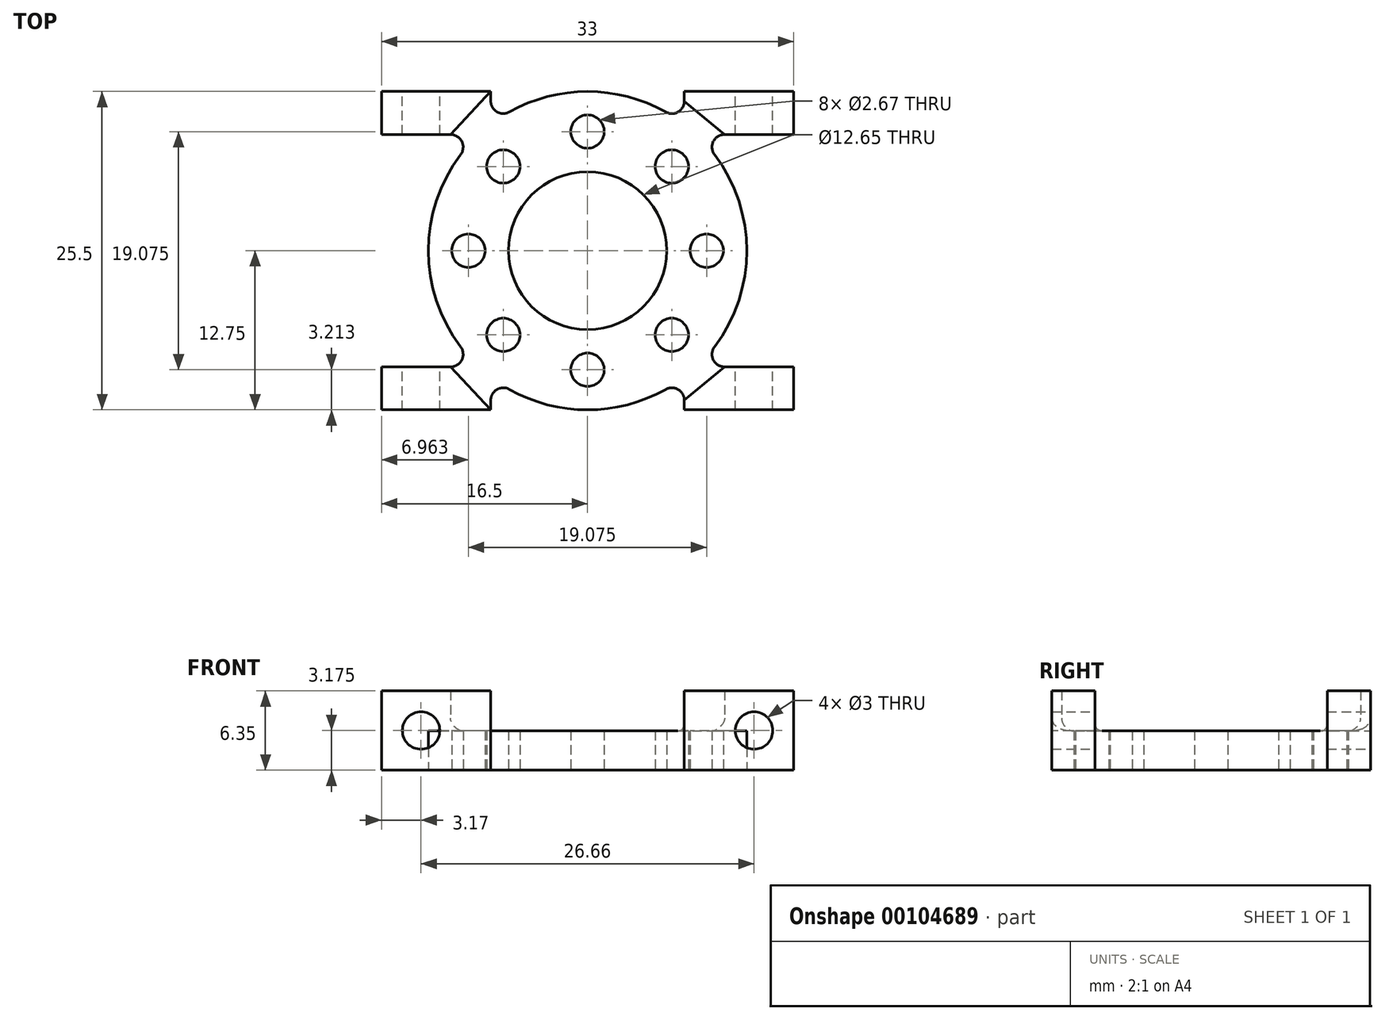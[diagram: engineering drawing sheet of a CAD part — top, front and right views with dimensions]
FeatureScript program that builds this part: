
annotation { "Feature Type Name" : "Feature", "Feature Type Description" : "" }
export const myFeature = defineFeature(function(context is Context, id is Id, definition is map)
    precondition{}
    {
        {
            var Q0;
            Q0=qCreatedBy(makeId("Top.planeOp"),FACE);
            var sketch = newSketch(context, id + "F0", { "sketchPlane" : qUnion([Q0])});
            skCircle(sketch, "E0", {"center": v(0, 0) * mm, "radius": 12.75 * mm});
            skCircle(sketch, "E1", {"center": v(0, 0) * mm, "radius": 6.33 * mm});
            skLineSegment(sketch, "E2", {"start": v(0, 6.33) * mm, "end": v(0, 12.75) * mm, "construction": true});
            skCircle(sketch, "E3", {"center": v(0, 9.54) * mm, "radius": 1.33 * mm});
            skCircle(sketch, "E4.1.0", {"center": v(-6.74, 6.74) * mm, "radius": 1.33 * mm});
            skCircle(sketch, "E4.2.0", {"center": v(-9.54, 0) * mm, "radius": 1.33 * mm});
            skCircle(sketch, "E4.3.0", {"center": v(-6.74, -6.74) * mm, "radius": 1.33 * mm});
            skCircle(sketch, "E4.4.0", {"center": v(0, -9.54) * mm, "radius": 1.33 * mm});
            skCircle(sketch, "E4.5.0", {"center": v(6.74, -6.74) * mm, "radius": 1.33 * mm});
            skCircle(sketch, "E4.6.0", {"center": v(9.54, 0) * mm, "radius": 1.33 * mm});
            skCircle(sketch, "E4.7.0", {"center": v(6.74, 6.74) * mm, "radius": 1.33 * mm});
            skSolve(sketch);
        }
        {
            var Q0;
            Q0 = qSketchRegion(id + "F0", true);
            extrude(context, id + "F1", {"entities" : qUnion([Q0]), "depth" : 3.15 * mm});
        }
        {
            var Q0;
            Q0=qCreatedBy(makeId("Top.planeOp"),FACE);
            var sketch = newSketch(context, id + "F2", { "sketchPlane" : qUnion([Q0])});
            skLineSegment(sketch, "E5.bottom", {"start": v(7.75, 12.75) * mm, "end": v(16.5, 12.75) * mm});
            skLineSegment(sketch, "E5.top", {"start": v(10.96, 9.3) * mm, "end": v(16.5, 9.3) * mm});
            skLineSegment(sketch, "E5.left", {"start": v(7.75, 12.75) * mm, "end": v(7.75, 11.98) * mm});
            skLineSegment(sketch, "E5.right", {"start": v(16.5, 12.75) * mm, "end": v(16.5, 9.3) * mm});
            skLineSegment(sketch, "E6.bottom", {"start": v(10.96, -9.3) * mm, "end": v(16.5, -9.3) * mm});
            skLineSegment(sketch, "E6.top", {"start": v(7.75, -12.75) * mm, "end": v(16.5, -12.75) * mm});
            skLineSegment(sketch, "E6.left", {"start": v(7.75, -11.98) * mm, "end": v(7.75, -12.75) * mm});
            skLineSegment(sketch, "E6.right", {"start": v(16.5, -9.3) * mm, "end": v(16.5, -12.75) * mm});
            skLineSegment(sketch, "E7.bottom", {"start": v(-16.5, 12.75) * mm, "end": v(-7.75, 12.75) * mm});
            skLineSegment(sketch, "E7.top", {"start": v(-16.5, 9.3) * mm, "end": v(-10.96, 9.3) * mm});
            skLineSegment(sketch, "E7.left", {"start": v(-16.5, 12.75) * mm, "end": v(-16.5, 9.3) * mm});
            skLineSegment(sketch, "E7.right", {"start": v(-7.75, 12.75) * mm, "end": v(-7.75, 11.98) * mm});
            skLineSegment(sketch, "E8.bottom", {"start": v(-16.5, -9.3) * mm, "end": v(-10.96, -9.3) * mm});
            skLineSegment(sketch, "E8.top", {"start": v(-16.5, -12.75) * mm, "end": v(-7.75, -12.75) * mm});
            skLineSegment(sketch, "E8.left", {"start": v(-16.5, -9.3) * mm, "end": v(-16.5, -12.75) * mm});
            skLineSegment(sketch, "E8.right", {"start": v(-7.75, -11.98) * mm, "end": v(-7.75, -12.75) * mm});
            skPoint(sketch, "E9.visualSharp", {"position": v(-7.75, 10.12) * mm});
            skArc(sketch, "E9.filletArc", {"start": v(-7.75, 11.98) * mm, "mid": v(-7.25, 11.12) * mm, "end": v(-6.26, 11.1) * mm});
            skPoint(sketch, "E10.visualSharp", {"position": v(-8.72, 9.3) * mm});
            skArc(sketch, "E10.filletArc", {"start": v(-10.17, 7.7) * mm, "mid": v(-10.07, 8.75) * mm, "end": v(-10.96, 9.3) * mm});
            skPoint(sketch, "E11.visualSharp", {"position": v(7.75, 10.12) * mm});
            skArc(sketch, "E11.filletArc", {"start": v(6.26, 11.1) * mm, "mid": v(7.25, 11.12) * mm, "end": v(7.75, 11.98) * mm});
            skPoint(sketch, "E12.visualSharp", {"position": v(8.72, 9.3) * mm});
            skArc(sketch, "E12.filletArc", {"start": v(10.96, 9.3) * mm, "mid": v(10.07, 8.75) * mm, "end": v(10.17, 7.7) * mm});
            skPoint(sketch, "E13.visualSharp", {"position": v(8.72, -9.3) * mm});
            skArc(sketch, "E13.filletArc", {"start": v(10.17, -7.7) * mm, "mid": v(10.07, -8.75) * mm, "end": v(10.96, -9.3) * mm});
            skPoint(sketch, "E14.visualSharp", {"position": v(7.75, -10.12) * mm});
            skArc(sketch, "E14.filletArc", {"start": v(7.75, -11.98) * mm, "mid": v(7.25, -11.12) * mm, "end": v(6.26, -11.1) * mm});
            skPoint(sketch, "E15.visualSharp", {"position": v(-8.72, -9.3) * mm});
            skArc(sketch, "E15.filletArc", {"start": v(-10.96, -9.3) * mm, "mid": v(-10.07, -8.75) * mm, "end": v(-10.17, -7.7) * mm});
            skPoint(sketch, "E16.visualSharp", {"position": v(-7.75, -10.12) * mm});
            skArc(sketch, "E16.filletArc", {"start": v(-6.26, -11.1) * mm, "mid": v(-7.25, -11.12) * mm, "end": v(-7.75, -11.98) * mm});
            skArc(sketch, "E17", {"start": v(-10.17, 7.7) * mm, "mid": v(-8.39, 9.6) * mm, "end": v(-6.26, 11.1) * mm});
            skArc(sketch, "E18", {"start": v(6.26, 11.1) * mm, "mid": v(8.39, 9.6) * mm, "end": v(10.17, 7.7) * mm});
            skArc(sketch, "E19", {"start": v(-10.17, -7.7) * mm, "mid": v(-8.39, -9.6) * mm, "end": v(-6.26, -11.1) * mm});
            skArc(sketch, "E20", {"start": v(6.26, -11.1) * mm, "mid": v(8.39, -9.6) * mm, "end": v(10.17, -7.7) * mm});
            skSolve(sketch);
        }
        {
            var Q0;
            Q0 = qSketchRegion(id + "F2", true);
            extrude(context, id + "F3", {"entities" : qUnion([Q0]), "operationType" : NewBodyOperationType.ADD, "depth" : 6.35 * mm});
        }
        {
            var Q0;
            Q0=makeQuery(id+"F3.opExtrude","CAP_FACE",FACE,{"disambiguationData":[OSD([sQuery(id+"F2.wireOp",EDGE,"E5.bottom"),sQuery(id+"F2.wireOp",EDGE,"E5.top"),sQuery(id+"F2.wireOp",EDGE,"E5.left"),sQuery(id+"F2.wireOp",EDGE,"E5.right"),sQuery(id+"F2.wireOp",EDGE,"E11.filletArc"),sQuery(id+"F2.wireOp",EDGE,"E12.filletArc"),sQuery(id+"F2.wireOp",EDGE,"E18")])],"isStart":false});
            var sketch = newSketch(context, id + "F4", { "sketchPlane" : qUnion([Q0])});
            skLineSegment(sketch, "E21", {"start": v(7.75, 11.98) * mm, "end": v(6.26, 11.1) * mm});
            skLineSegment(sketch, "E22", {"start": v(6.26, 11.1) * mm, "end": v(10.17, 7.7) * mm});
            skLineSegment(sketch, "E23", {"start": v(10.17, 7.7) * mm, "end": v(10.96, 9.3) * mm});
            skLineSegment(sketch, "E24", {"start": v(10.96, 9.3) * mm, "end": v(7.75, 11.98) * mm});
            skLineSegment(sketch, "E25", {"start": v(-7.75, 12.75) * mm, "end": v(-6.26, 11.1) * mm});
            skLineSegment(sketch, "E26", {"start": v(-6.26, 11.1) * mm, "end": v(-10.17, 7.7) * mm});
            skLineSegment(sketch, "E27", {"start": v(-10.17, 7.7) * mm, "end": v(-10.96, 9.3) * mm});
            skLineSegment(sketch, "E28", {"start": v(-10.96, 9.3) * mm, "end": v(-7.75, 12.75) * mm});
            skLineSegment(sketch, "E29", {"start": v(10.17, -7.7) * mm, "end": v(10.96, -9.3) * mm});
            skLineSegment(sketch, "E30", {"start": v(10.96, -9.3) * mm, "end": v(7.75, -11.98) * mm});
            skLineSegment(sketch, "E31", {"start": v(7.75, -11.98) * mm, "end": v(6.26, -11.1) * mm});
            skLineSegment(sketch, "E32", {"start": v(6.26, -11.1) * mm, "end": v(10.17, -7.7) * mm});
            skLineSegment(sketch, "E33", {"start": v(-10.96, -9.3) * mm, "end": v(-10.17, -7.7) * mm});
            skLineSegment(sketch, "E34", {"start": v(-10.17, -7.7) * mm, "end": v(-6.26, -11.1) * mm});
            skLineSegment(sketch, "E35", {"start": v(-6.26, -11.1) * mm, "end": v(-7.75, -12.75) * mm});
            skLineSegment(sketch, "E36", {"start": v(-7.75, -12.75) * mm, "end": v(-10.96, -9.3) * mm});
            skSolve(sketch);
        }
        {
            var Q0;
            Q0 = qSketchRegion(id + "F4", true);
            var Q1;
            Q1=makeQuery(id+"F1.opExtrude","CAP_FACE",FACE,{"disambiguationData":[OSD([sQuery(id+"F0.wireOp",EDGE,"E0"),sQuery(id+"F0.wireOp",EDGE,"E1"),sQuery(id+"F0.wireOp",EDGE,"E3"),sQuery(id+"F0.wireOp",EDGE,"E4.1.0"),sQuery(id+"F0.wireOp",EDGE,"E4.2.0"),sQuery(id+"F0.wireOp",EDGE,"E4.3.0"),sQuery(id+"F0.wireOp",EDGE,"E4.4.0"),sQuery(id+"F0.wireOp",EDGE,"E4.5.0"),sQuery(id+"F0.wireOp",EDGE,"E4.6.0"),sQuery(id+"F0.wireOp",EDGE,"E4.7.0")])],"isStart":false});
            extrude(context, id + "F5", {"entities" : qUnion([Q0]), "operationType" : NewBodyOperationType.REMOVE, "endBound" : BoundingType.UP_TO_SURFACE, "oppositeDirection" : true, "endBoundEntityFace" : qUnion([Q1]), "depth" : 25 * mm});
        }
        {
            var Q0;
            Q0=makeQuery(id+"F5.boolean.opBoolean","COPY",EDGE,{"derivedFrom":makeQuery(id+"F5.opExtrude","CAP_EDGE",EDGE,{"disambiguationData":[OSD([sQuery(id+"F4.wireOp",EDGE,"E28")])],"isStart":false})});
            var Q1;
            Q1=makeQuery(id+"F5.boolean.opBoolean","COPY",EDGE,{"derivedFrom":makeQuery(id+"F5.opExtrude","CAP_EDGE",EDGE,{"disambiguationData":[OSD([sQuery(id+"F4.wireOp",EDGE,"E24")])],"isStart":false})});
            var Q2;
            Q2=makeQuery(id+"F5.boolean.opBoolean","COPY",EDGE,{"derivedFrom":makeQuery(id+"F5.opExtrude","CAP_EDGE",EDGE,{"disambiguationData":[OSD([sQuery(id+"F4.wireOp",EDGE,"E36")])],"isStart":false})});
            var Q3;
            Q3=makeQuery(id+"F5.boolean.opBoolean","COPY",EDGE,{"derivedFrom":makeQuery(id+"F5.opExtrude","CAP_EDGE",EDGE,{"disambiguationData":[OSD([sQuery(id+"F4.wireOp",EDGE,"E30")])],"isStart":false})});
            fillet(context, id + "F6", {"entities" : qUnion([Q0, Q1, Q2, Q3]), "radius" : 1 * mm, "tangentPropagation" : true, "allowEdgeOverflow" : false});
        }
        {
            var Q0;
            Q0=makeQuery(id+"F3.opExtrude","SWEPT_FACE",FACE,{"disambiguationData":[OSD([sQuery(id+"F2.wireOp",EDGE,"E7.bottom")])]});
            var sketch = newSketch(context, id + "F7", { "sketchPlane" : qUnion([Q0])});
            skCircle(sketch, "E37", {"center": v(13.33, 3.18) * mm, "radius": 1.5 * mm});
            skPoint(sketch, "E37.centerSnap0", {"position": v(16.5, 3.18) * mm});
            skCircle(sketch, "E38", {"center": v(-13.33, 3.18) * mm, "radius": 1.5 * mm});
            skSolve(sketch);
        }
        {
            var Q0;
            Q0 = qSketchRegion(id + "F7", true);
            extrude(context, id + "F8", {"entities" : qUnion([Q0]), "operationType" : NewBodyOperationType.REMOVE, "endBound" : BoundingType.THROUGH_ALL, "oppositeDirection" : true, "depth" : 25 * mm});
        }
        {
            var Q0;
            Q0=makeQuery(id+"F5.boolean.opBoolean","MERGE",FACE,{"derivedFrom":[makeQuery(id+"F1.opExtrude","CAP_FACE",FACE,{"disambiguationData":[OSD([sQuery(id+"F0.wireOp",EDGE,"E0"),sQuery(id+"F0.wireOp",EDGE,"E1"),sQuery(id+"F0.wireOp",EDGE,"E3"),sQuery(id+"F0.wireOp",EDGE,"E4.1.0"),sQuery(id+"F0.wireOp",EDGE,"E4.2.0"),sQuery(id+"F0.wireOp",EDGE,"E4.3.0"),sQuery(id+"F0.wireOp",EDGE,"E4.4.0"),sQuery(id+"F0.wireOp",EDGE,"E4.5.0"),sQuery(id+"F0.wireOp",EDGE,"E4.6.0"),sQuery(id+"F0.wireOp",EDGE,"E4.7.0")])],"isStart":false})],"fromTools":[makeQuery(id+"F5.opExtrude","CAP_FACE",FACE,{"disambiguationData":[OSD([sQuery(id+"F4.wireOp",EDGE,"E21"),sQuery(id+"F4.wireOp",EDGE,"E22"),sQuery(id+"F4.wireOp",EDGE,"E23"),sQuery(id+"F4.wireOp",EDGE,"E24")])],"isStart":false}),makeQuery(id+"F5.opExtrude","CAP_FACE",FACE,{"disambiguationData":[OSD([sQuery(id+"F4.wireOp",EDGE,"E25"),sQuery(id+"F4.wireOp",EDGE,"E26"),sQuery(id+"F4.wireOp",EDGE,"E27"),sQuery(id+"F4.wireOp",EDGE,"E28")])],"isStart":false}),makeQuery(id+"F5.opExtrude","CAP_FACE",FACE,{"disambiguationData":[OSD([sQuery(id+"F4.wireOp",EDGE,"E29"),sQuery(id+"F4.wireOp",EDGE,"E30"),sQuery(id+"F4.wireOp",EDGE,"E31"),sQuery(id+"F4.wireOp",EDGE,"E32")])],"isStart":false}),makeQuery(id+"F5.opExtrude","CAP_FACE",FACE,{"disambiguationData":[OSD([sQuery(id+"F4.wireOp",EDGE,"E33"),sQuery(id+"F4.wireOp",EDGE,"E34"),sQuery(id+"F4.wireOp",EDGE,"E35"),sQuery(id+"F4.wireOp",EDGE,"E36")])],"isStart":false})]});
            var sketch = newSketch(context, id + "F9", { "sketchPlane" : qUnion([Q0])});
            skArc(sketch, "E39", {"start": v(-11.83, 4.75) * mm, "mid": v(-12.75, 0) * mm, "end": v(-11.83, -4.75) * mm});
            skArc(sketch, "E40", {"start": v(11.83, 4.75) * mm, "mid": v(12.75, 0) * mm, "end": v(11.83, -4.75) * mm});
            skLineSegment(sketch, "E41", {"start": v(-11.83, 4.75) * mm, "end": v(-11.83, -4.75) * mm});
            skLineSegment(sketch, "E42", {"start": v(11.83, -4.75) * mm, "end": v(11.83, 4.75) * mm});
            skSolve(sketch);
        }
        {
            var Q0;
            Q0 = qSketchRegion(id + "F9", true);
            var Q1;
            Q1=makeQuery(id+"F3.boolean.opBoolean","MERGE",FACE,{"derivedFrom":[makeQuery(id+"F1.opExtrude","CAP_FACE",FACE,{"disambiguationData":[OSD([sQuery(id+"F0.wireOp",EDGE,"E0"),sQuery(id+"F0.wireOp",EDGE,"E1"),sQuery(id+"F0.wireOp",EDGE,"E3"),sQuery(id+"F0.wireOp",EDGE,"E4.1.0"),sQuery(id+"F0.wireOp",EDGE,"E4.2.0"),sQuery(id+"F0.wireOp",EDGE,"E4.3.0"),sQuery(id+"F0.wireOp",EDGE,"E4.4.0"),sQuery(id+"F0.wireOp",EDGE,"E4.5.0"),sQuery(id+"F0.wireOp",EDGE,"E4.6.0"),sQuery(id+"F0.wireOp",EDGE,"E4.7.0")])],"isStart":true}),makeQuery(id+"F3.opExtrude","CAP_FACE",FACE,{"disambiguationData":[OSD([sQuery(id+"F2.wireOp",EDGE,"E5.bottom"),sQuery(id+"F2.wireOp",EDGE,"E5.top"),sQuery(id+"F2.wireOp",EDGE,"E5.left"),sQuery(id+"F2.wireOp",EDGE,"E5.right"),sQuery(id+"F2.wireOp",EDGE,"E11.filletArc"),sQuery(id+"F2.wireOp",EDGE,"E12.filletArc"),sQuery(id+"F2.wireOp",EDGE,"E18")])],"isStart":true}),makeQuery(id+"F3.opExtrude","CAP_FACE",FACE,{"disambiguationData":[OSD([sQuery(id+"F2.wireOp",EDGE,"E6.bottom"),sQuery(id+"F2.wireOp",EDGE,"E6.top"),sQuery(id+"F2.wireOp",EDGE,"E6.left"),sQuery(id+"F2.wireOp",EDGE,"E6.right"),sQuery(id+"F2.wireOp",EDGE,"E13.filletArc"),sQuery(id+"F2.wireOp",EDGE,"E14.filletArc"),sQuery(id+"F2.wireOp",EDGE,"E20")])],"isStart":true}),makeQuery(id+"F3.opExtrude","CAP_FACE",FACE,{"disambiguationData":[OSD([sQuery(id+"F2.wireOp",EDGE,"E7.bottom"),sQuery(id+"F2.wireOp",EDGE,"E7.top"),sQuery(id+"F2.wireOp",EDGE,"E7.left"),sQuery(id+"F2.wireOp",EDGE,"E7.right"),sQuery(id+"F2.wireOp",EDGE,"E9.filletArc"),sQuery(id+"F2.wireOp",EDGE,"E10.filletArc"),sQuery(id+"F2.wireOp",EDGE,"E17")])],"isStart":true}),makeQuery(id+"F3.opExtrude","CAP_FACE",FACE,{"disambiguationData":[OSD([sQuery(id+"F2.wireOp",EDGE,"E8.bottom"),sQuery(id+"F2.wireOp",EDGE,"E8.top"),sQuery(id+"F2.wireOp",EDGE,"E8.left"),sQuery(id+"F2.wireOp",EDGE,"E8.right"),sQuery(id+"F2.wireOp",EDGE,"E15.filletArc"),sQuery(id+"F2.wireOp",EDGE,"E16.filletArc"),sQuery(id+"F2.wireOp",EDGE,"E19")])],"isStart":true})]});
            extrude(context, id + "F10", {"entities" : qUnion([Q0]), "operationType" : NewBodyOperationType.ADD, "endBound" : BoundingType.UP_TO_SURFACE, "oppositeDirection" : true, "endBoundEntityFace" : qUnion([Q1]), "depth" : 25 * mm});
        }
    });
